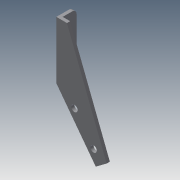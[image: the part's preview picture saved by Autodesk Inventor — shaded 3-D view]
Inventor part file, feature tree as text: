
AUTODESK INVENTOR PART (.ipt)
format: ipt  version: 2013 (Build 170138000, 138)  size: 153,088 bytes
history: native  units: mm
features: sketch x12, extrude x7, fillet x2
ambient origin geometry x8: Origin, YZ Plane, XZ Plane, XY Plane, X Axis, Y Axis, Z Axis, Center Point
bodies: Solid1 (feature_tree)
feature tree (21):
  sketch  "Sketch1"  dims[d4=3.0mm d5=3.0mm d6=2.0mm d7=0.0mm]
  extrude  "Extrusion1"  Depth=2.0mm TaperAngle=0.0deg
  extrude  "Extrusion2"  Depth=2.0mm TaperAngle=0.0deg
  extrude  "Extrusion3"  Depth=2.0mm TaperAngle=0.0deg
  sketch  "Sketch5"  dims[d21=10.0mm d22=0.0mm d23=0.5mm d24=0.0mm]
  extrude  "Extrusion4"  Depth=6.0mm TaperAngle=0.0deg
  sketch  "Sketch7"  dims[d28=2.0mm]
  sketch  "Sketch8"
  extrude  "Extrusion5"  Depth=0.5mm TaperAngle=0.0deg
  extrude  "Extrusion6"  Depth=2.0mm
  extrude  "Extrusion7"  [1 undecoded]
  fillet  "Fillet1"  [1 undecoded]
  fillet  "Fillet2"  [1 undecoded]
  sketch  "Sketch12"
  sketch  "Sketch2"  dims[d8=10.0mm d11=2.0mm d12=0.0mm]
  sketch  "Sketch3"  dims[d13=5.0mm d14=2.0mm d15=0.0mm]
  sketch  "Sketch4"  dims[d16=2.0mm d17=6.0mm d18=0.0mm]
  sketch  "Sketch6"  dims[d25=0.5mm d26=0.0mm d27=2.0mm]
  sketch  "Sketch9"
  sketch  "Sketch10"
  sketch  "Sketch11"
note: 3 required parameter values undecoded (feature->parameter linkage not recoverable at this tier; creation-order binding heuristic only, values carry confidence <= 0.55)
